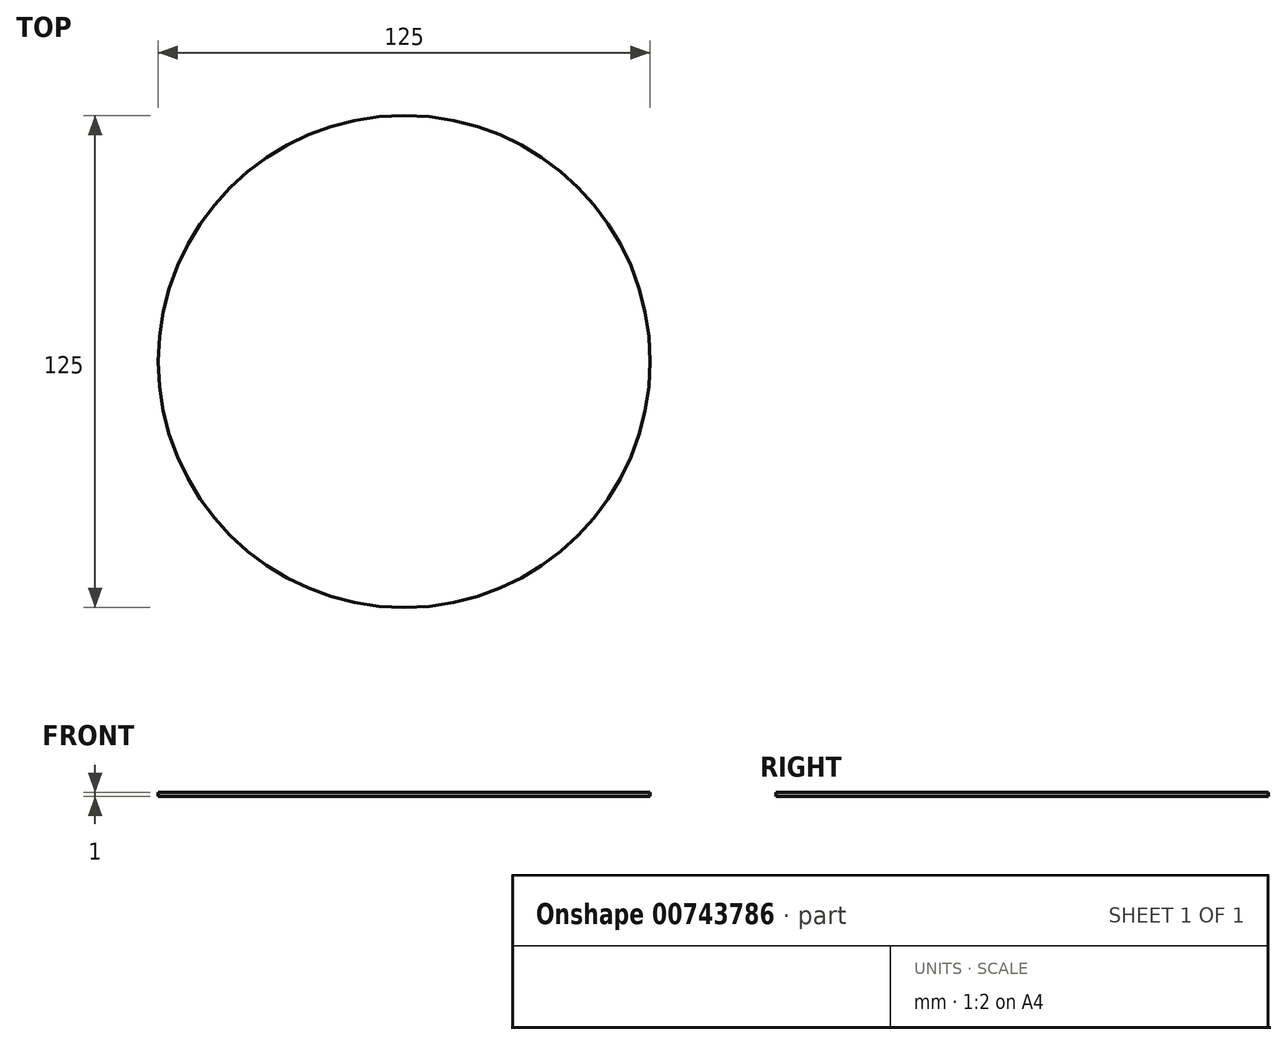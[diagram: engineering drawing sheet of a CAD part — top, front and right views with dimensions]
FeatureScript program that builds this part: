
annotation { "Feature Type Name" : "Feature", "Feature Type Description" : "" }
export const myFeature = defineFeature(function(context is Context, id is Id, definition is map)
    precondition{}
    {
        {
            var Q0;
            Q0=qCreatedBy(makeId("Top.planeOp"),FACE);
            var sketch = newSketch(context, id + "F0", { "sketchPlane" : qUnion([Q0])});
            skCircle(sketch, "E0", {"center": v(0, 0) * mm, "radius": 62.5 * mm});
            skSolve(sketch);
        }
        {
            var Q0;
            Q0=makeQuery(id+"F0.imprint","IMPRINT",FACE,{"disambiguationData":[TD([[makeQuery(id+"F0.imprint","IMPRINT",EDGE,{"derivedFrom":sQuery(id+"F0.wireOp",EDGE,"E0")}),1.0]])]});
            extrude(context, id + "F1", {"entities" : qUnion([Q0]), "oppositeDirection" : true, "depth" : 1 * mm, "offsetDistance" : 25 * mm});
        }
    });
